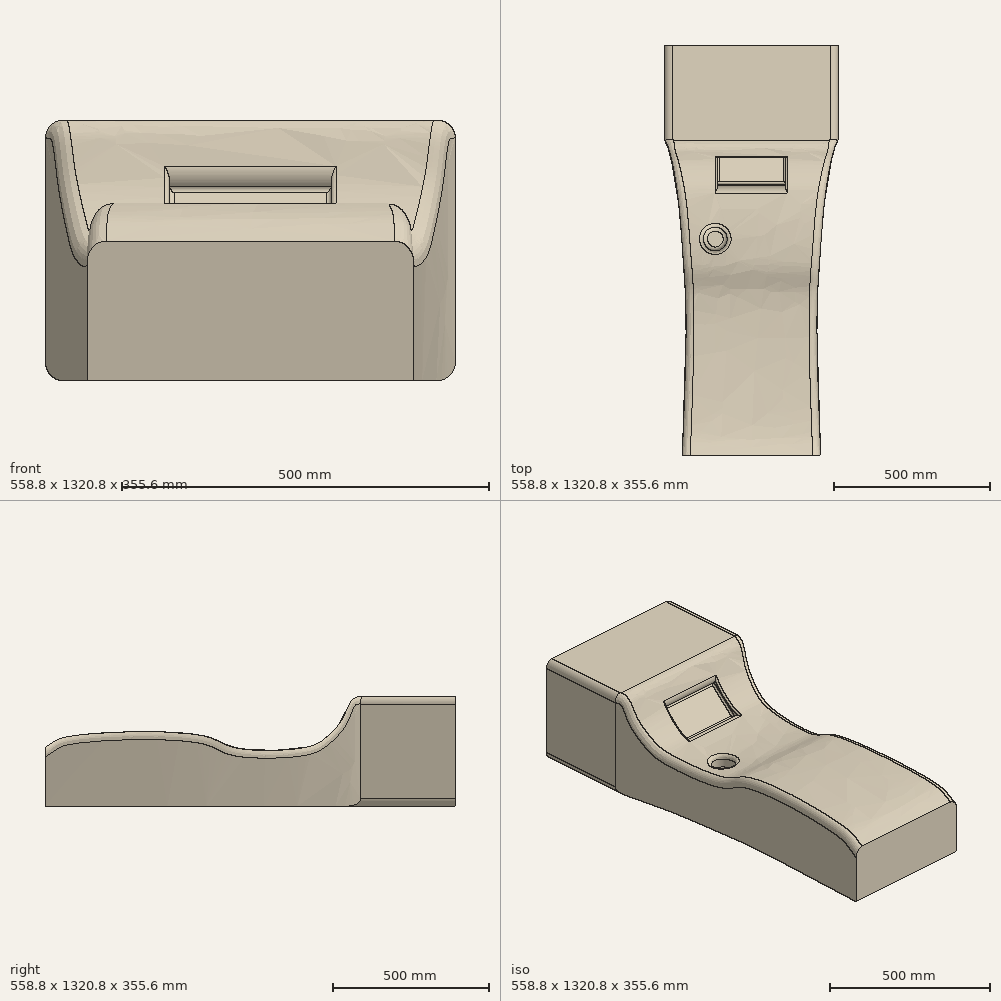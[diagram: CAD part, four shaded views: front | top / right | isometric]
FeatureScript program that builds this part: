
annotation { "Feature Type Name" : "Feature", "Feature Type Description" : "" }
export const myFeature = defineFeature(function(context is Context, id is Id, definition is map)
    precondition{}
    {
        {
            var Q0;
            Q0=qCreatedBy(makeId("Front.planeOp"),FACE);
            cPlane(context, id + "F0", {"entities" : qUnion([Q0]), "cplaneType" : CPlaneType.OFFSET, "offset" : 1016 * mm, "oppositeDirection" : true, "width" : 152.4 * mm, "height" : 152.4 * mm});
        }
        {
            var Q0;
            Q0=qCreatedBy(id+"F0.planeOp",FACE);
            var sketch = newSketch(context, id + "F1", { "sketchPlane" : qUnion([Q0])});
            skPoint(sketch, "E0.0", {"position": v(0, 165.1) * mm});
            skLineSegment(sketch, "E1", {"start": v(0, 165.1) * mm, "end": v(279.4, 165.1) * mm});
            skLineSegment(sketch, "E2", {"start": v(279.4, 165.1) * mm, "end": v(279.4, -190.5) * mm});
            skLineSegment(sketch, "E3", {"start": v(279.4, -190.5) * mm, "end": v(0, -190.5) * mm});
            skLineSegment(sketch, "E4", {"start": v(0, 165.1) * mm, "end": v(-279.4, 165.1) * mm});
            skLineSegment(sketch, "E5", {"start": v(-279.4, 165.1) * mm, "end": v(-279.4, -190.5) * mm});
            skLineSegment(sketch, "E6", {"start": v(-279.4, -190.5) * mm, "end": v(0, -190.5) * mm});
            skSolve(sketch);
        }
        {
            var Q0;
            Q0=qCreatedBy(makeId("Right.planeOp"),FACE);
            var sketch = newSketch(context, id + "F2", { "sketchPlane" : qUnion([Q0])});
            skFitSpline(sketch, "E7", {"points": [v(0, 0) * mm, v(24.74, 16.6) * mm, v(49, 28.94) * mm, v(187.46, 47.43) * mm, v(521.37, 34.71) * mm, v(607.94, 0) * mm, v(838.07, 0) * mm, v(901.63, 29.24) * mm, v(960.8, 98.27) * mm, v(1016, 165.1) * mm], "startDerivative": vector(273.3, 180.11) * mm, "endDerivative": vector(1078.66, 86.3) * mm});
            skLineSegment(sketch, "E8", {"start": v(0, 0) * mm, "end": v(0, 310.78) * mm});
            skLineSegment(sketch, "E9", {"start": v(0, 310.78) * mm, "end": v(1016, 310.78) * mm});
            skLineSegment(sketch, "E10", {"start": v(1016, 310.78) * mm, "end": v(1016, 165.1) * mm});
            skSolve(sketch);
        }
        {
            var Q0;
            Q0 = qSketchRegion(id + "F1", true);
            extrude(context, id + "F3", {"entities" : qUnion([Q0]), "depth" : 1016 * mm, "offsetDistance" : 25.4 * mm});
        }
        {
            var Q0;
            Q0=makeQuery(id+"F2.imprint","IMPRINT",FACE,{"disambiguationData":[TD([[makeQuery(id+"F2.imprint","IMPRINT",EDGE,{"derivedFrom":sQuery(id+"F2.wireOp",EDGE,"E7")}),1.0]])]});
            extrude(context, id + "F4", {"entities" : qUnion([Q0]), "operationType" : NewBodyOperationType.REMOVE, "endBound" : BoundingType.SYMMETRIC, "depth" : 1016 * mm, "offsetDistance" : 25.4 * mm});
        }
        {
            var Q0;
            Q0=qCreatedBy(makeId("Top.planeOp"),FACE);
            var sketch = newSketch(context, id + "F5", { "sketchPlane" : qUnion([Q0])});
            skLineSegment(sketch, "E11", {"start": v(279.4, 1016) * mm, "end": v(-279.4, 1016) * mm});
            skPoint(sketch, "E12.0", {"position": v(-222.79, 0) * mm});
            skLineSegment(sketch, "E13", {"start": v(0, 0) * mm, "end": v(-222.79, 0) * mm});
            skFitSpline(sketch, "E14", {"points": [v(-222.79, 0) * mm, v(-210.88, 448.78) * mm, v(-222.09, 661.6) * mm, v(-238.88, 845.63) * mm, v(-279.4, 1016) * mm], "startDerivative": vector(40.64, 1158.52) * mm, "endDerivative": vector(-221.68, 293.58) * mm});
            skLineSegment(sketch, "E15", {"start": v(-279.4, 1016) * mm, "end": v(-279.4, 0) * mm});
            skLineSegment(sketch, "E16", {"start": v(-222.79, 0) * mm, "end": v(-279.4, 0) * mm});
            skLineSegment(sketch, "E17.0", {"start": v(279.4, 0) * mm, "end": v(-279.4, 0) * mm});
            skFitSpline(sketch, "E18.0", {"points": [v(279.4, 1016) * mm, v(279.4, 979.93) * mm, v(279.4, 970.1) * mm, v(279.4, 900.22) * mm, v(279.4, 844.06) * mm, v(279.4, 591.76) * mm, v(279.4, 534.2) * mm, v(279.4, 191.24) * mm, v(279.4, 51.87) * mm, v(279.4, 26.72) * mm, v(279.4, 5.36) * mm, v(279.4, 0) * mm]});
            skFitSpline(sketch, "E19.MirrorCS", {"points": [v(222.79, 0) * mm, v(210.88, 448.78) * mm, v(222.09, 661.6) * mm, v(238.88, 845.63) * mm, v(279.4, 1016) * mm], "startDerivative": vector(-40.64, 1158.52) * mm, "endDerivative": vector(221.68, 293.58) * mm});
            skSolve(sketch);
        }
        {
            var Q0;
            {var subQ0=sQuery(id+"F5.wireOp",EDGE,"E14");Q0=makeQuery(id+"F5.imprint","IMPRINT",FACE,{"disambiguationData":[TD([[makeQuery(id+"F5.imprint","IMPRINT",EDGE,{"derivedFrom":subQ0}),1.0]])]});}
            var Q1;
            {var subQ0=sQuery(id+"F5.wireOp",EDGE,"E18.0");Q1=makeQuery(id+"F5.imprint","IMPRINT",FACE,{"disambiguationData":[TD([[makeQuery(id+"F5.imprint","IMPRINT",EDGE,{"derivedFrom":subQ0}),-1.0]])]});}
            extrude(context, id + "F6", {"entities" : qUnion([Q0, Q1]), "operationType" : NewBodyOperationType.REMOVE, "endBound" : BoundingType.SYMMETRIC, "oppositeDirection" : true, "depth" : 508 * mm, "offsetDistance" : 25.4 * mm});
        }
        {
            var Q0;
            Q0=makeQuery(id+"F1.imprint","IMPRINT",FACE,{"disambiguationData":[TD([[makeQuery(id+"F1.imprint","IMPRINT",EDGE,{"derivedFrom":sQuery(id+"F1.wireOp",EDGE,"E1")}),-1.0]])]});
            var sketch = newSketch(context, id + "F7", { "sketchPlane" : qUnion([Q0])});
            skLineSegment(sketch, "E20.0", {"start": v(0, 165.1) * mm, "end": v(279.4, 165.1) * mm});
            skLineSegment(sketch, "E21.0", {"start": v(0, 165.1) * mm, "end": v(-279.4, 165.1) * mm});
            skLineSegment(sketch, "E22.0", {"start": v(-279.4, 165.1) * mm, "end": v(-279.4, -190.5) * mm});
            skLineSegment(sketch, "E23.0", {"start": v(-279.4, -190.5) * mm, "end": v(0, -190.5) * mm});
            skLineSegment(sketch, "E24.0", {"start": v(279.4, -190.5) * mm, "end": v(0, -190.5) * mm});
            skLineSegment(sketch, "E25.0", {"start": v(279.4, 165.1) * mm, "end": v(279.4, -190.5) * mm});
            skLineSegment(sketch, "E26.bottom", {"start": v(279.4, 165.1) * mm, "end": v(-279.4, 165.1) * mm});
            skLineSegment(sketch, "E26.top", {"start": v(279.4, -190.5) * mm, "end": v(-279.4, -190.5) * mm});
            skSolve(sketch);
        }
        {
            var Q0;
            {var subQ3=sQuery(id+"F7.wireOp",EDGE,"E25.0");Q0=makeQuery(id+"F7.imprint","IMPRINT",FACE,{"disambiguationData":[TD([[makeQuery(id+"F7.imprint","IMPRINT",EDGE,{"derivedFrom":subQ3}),-1.0]])]});}
            extrude(context, id + "F8", {"entities" : qUnion([Q0]), "operationType" : NewBodyOperationType.ADD, "oppositeDirection" : true, "depth" : 304.8 * mm, "offsetDistance" : 25.4 * mm});
        }
        {
            var Q0;
            Q0=makeQuery(id+"F8.opExtrude","SWEPT_EDGE",EDGE,{"disambiguationData":[OSD([sQuery(id+"F7.wireOp",EDGE,"E26.bottom"),sQuery(id+"F7.wireOp",EDGE,"E22.0")])]});
            var Q1;
            Q1=makeQuery(id+"F6.boolean.opBoolean","INTERSECT",EDGE,{"derivedFrom":[makeQuery(id+"F4.boolean.opBoolean","COPY",FACE,{"derivedFrom":makeQuery(id+"F4.opExtrude","SWEPT_FACE",FACE,{"disambiguationData":[OSD([sQuery(id+"F2.wireOp",EDGE,"E7")])]})}),makeQuery(id+"F6.opExtrude","SWEPT_FACE",FACE,{"disambiguationData":[OSD([sQuery(id+"F5.wireOp",EDGE,"E14")])]})]});
            var Q2;
            Q2=makeQuery(id+"F8.opExtrude","SWEPT_EDGE",EDGE,{"disambiguationData":[OSD([sQuery(id+"F7.wireOp",EDGE,"E26.bottom"),sQuery(id+"F7.wireOp",EDGE,"E25.0")])]});
            var Q3;
            Q3=makeQuery(id+"F6.boolean.opBoolean","INTERSECT",EDGE,{"derivedFrom":[makeQuery(id+"F4.boolean.opBoolean","COPY",FACE,{"derivedFrom":makeQuery(id+"F4.opExtrude","SWEPT_FACE",FACE,{"disambiguationData":[OSD([sQuery(id+"F2.wireOp",EDGE,"E7")])]})}),makeQuery(id+"F6.opExtrude","SWEPT_FACE",FACE,{"disambiguationData":[OSD([sQuery(id+"F5.wireOp",EDGE,"E19.MirrorCS")])]})]});
            var Q4;
            Q4=makeQuery(id+"F4.boolean.opBoolean","COPY",EDGE,{"derivedFrom":makeQuery(id+"F4.opExtrude","SWEPT_EDGE",EDGE,{"disambiguationData":[OSD([sQuery(id+"F2.wireOp",EDGE,"E7"),sQuery(id+"F2.wireOp",EDGE,"E8")])]})});
            var Q5;
            Q5=makeQuery(id+"F6.boolean.opBoolean","COPY",EDGE,{"derivedFrom":makeQuery(id+"F6.opExtrude","SWEPT_EDGE",EDGE,{"disambiguationData":[OSD([sQuery(id+"F5.wireOp",EDGE,"E17.0"),sQuery(id+"F5.wireOp",EDGE,"E19.MirrorCS")])]})});
            var Q6;
            Q6=makeQuery(id+"F6.boolean.opBoolean","COPY",EDGE,{"derivedFrom":makeQuery(id+"F6.opExtrude","SWEPT_EDGE",EDGE,{"disambiguationData":[OSD([sQuery(id+"F5.wireOp",EDGE,"E14"),sQuery(id+"F5.wireOp",EDGE,"E17.0")])]})});
            fillet(context, id + "F9", {"entities" : qUnion([Q0, Q1, Q2, Q3, Q4, Q5, Q6]), "radius" : 25.4 * mm, "tangentPropagation" : true, "allowEdgeOverflow" : false});
        }
        {
            var Q0;
            Q0=qCreatedBy(makeId("Top.planeOp"),FACE);
            var sketch = newSketch(context, id + "F10", { "sketchPlane" : qUnion([Q0])});
            skLineSegment(sketch, "E27", {"start": v(-218, 696.98) * mm, "end": v(214.2, 696.98) * mm, "construction": true});
            skCircle(sketch, "E28", {"center": v(-116.4, 696.98) * mm, "radius": 38.1 * mm});
            skLineSegment(sketch, "E29.0", {"start": v(-196.46, 11.18) * mm, "end": v(196.46, 11.18) * mm});
            skSolve(sketch);
        }
        {
            var Q0;
            Q0 = qSketchRegion(id + "F10", true);
            extrude(context, id + "F11", {"entities" : qUnion([Q0]), "operationType" : NewBodyOperationType.REMOVE, "oppositeDirection" : true, "depth" : 63.5 * mm, "offsetDistance" : 25.4 * mm});
        }
        {
            var Q0;
            Q0=makeQuery(id+"F11.boolean.opBoolean","INTERSECT",EDGE,{"derivedFrom":[makeQuery(id+"F4.boolean.opBoolean","COPY",FACE,{"derivedFrom":makeQuery(id+"F4.opExtrude","SWEPT_FACE",FACE,{"disambiguationData":[OSD([sQuery(id+"F2.wireOp",EDGE,"E7")])]})}),makeQuery(id+"F11.opExtrude","SWEPT_FACE",FACE,{"disambiguationData":[OSD([sQuery(id+"F10.wireOp",EDGE,"E28")])]})]});
            var Q1;
            Q1=makeQuery(id+"F11.boolean.opBoolean","COPY",EDGE,{"derivedFrom":makeQuery(id+"F11.opExtrude","CAP_EDGE",EDGE,{"disambiguationData":[OSD([sQuery(id+"F10.wireOp",EDGE,"E28")])],"isStart":false})});
            var Q2;
            Q2=makeQuery(id+"FA7N4mf670c91CE_1.1.F11.boolean.opBoolean","INTERSECT",EDGE,{"derivedFrom":[makeQuery(id+"F4.boolean.opBoolean","COPY",FACE,{"derivedFrom":makeQuery(id+"F4.opExtrude","SWEPT_FACE",FACE,{"disambiguationData":[OSD([sQuery(id+"F2.wireOp",EDGE,"E7")])]})}),makeQuery(id+"FA7N4mf670c91CE_1.1.F11.opExtrude","SWEPT_FACE",FACE,{"disambiguationData":[OSD([sQuery(id+"F10.wireOp",EDGE,"E28")])]})]});
            var Q3;
            Q3=makeQuery(id+"FA7N4mf670c91CE_1.1.F11.boolean.opBoolean","COPY",EDGE,{"derivedFrom":makeQuery(id+"FA7N4mf670c91CE_1.1.F11.opExtrude","CAP_EDGE",EDGE,{"disambiguationData":[OSD([sQuery(id+"F10.wireOp",EDGE,"E28")])],"isStart":false})});
            fillet(context, id + "F12", {"entities" : qUnion([Q0, Q1, Q2, Q3]), "radius" : 12.7 * mm, "tangentPropagation" : true, "allowEdgeOverflow" : false});
        }
        {
            var Q0;
            Q0=sQuery(id+"F1.wireOp",EDGE,"E1");
            cPoint(context, id + "F13", {"entities" : qUnion([Q0]), "parameter" : 0.5});
        }
        {
            var Q0;
            Q0=sQuery(id+"F1.wireOp",EDGE,"E4");
            cPoint(context, id + "F14", {"entities" : qUnion([Q0]), "parameter" : 0.5});
        }
        {
            var Q0;
            Q0 = qCreatedBy(id + "F13" ,VERTEX);
            var Q1;
            Q1 = qCreatedBy(id + "F14" ,VERTEX);
            var Q2;
            Q2=sQuery(id+"F2.wireOp",VERTEX,"E7.6.internal");
            cPlane(context, id + "F15", {"entities" : qUnion([Q0, Q1, Q2]), "cplaneType" : CPlaneType.THREE_POINT, "offset" : 25.4 * mm, "width" : 152.4 * mm, "height" : 152.4 * mm});
        }
        {
            var Q0;
            Q0=qCreatedBy(id+"F15.planeOp",FACE);
            var sketch = newSketch(context, id + "F16", { "sketchPlane" : qUnion([Q0])});
            skLineSegment(sketch, "E30.bottom", {"start": v(-110.5, -758.55) * mm, "end": v(110.5, -758.55) * mm});
            skLineSegment(sketch, "E30.top", {"start": v(-110.5, -633.32) * mm, "end": v(110.5, -633.32) * mm});
            skLineSegment(sketch, "E30.left", {"start": v(-110.49, -758.55) * mm, "end": v(-110.5, -633.32) * mm});
            skLineSegment(sketch, "E30.right", {"start": v(110.5, -758.55) * mm, "end": v(110.5, -633.32) * mm});
            skSolve(sketch);
        }
        {
            var Q0;
            Q0 = qSketchRegion(id + "F16", true);
            extrude(context, id + "F17", {"entities" : qUnion([Q0]), "operationType" : NewBodyOperationType.REMOVE, "depth" : 38.1 * mm, "offsetDistance" : 25.4 * mm});
        }
        {
            var Q0;
            Q0=makeQuery(id+"F17.boolean.opBoolean","INTERSECT",EDGE,{"derivedFrom":[makeQuery(id+"F4.boolean.opBoolean","COPY",FACE,{"derivedFrom":makeQuery(id+"F4.opExtrude","SWEPT_FACE",FACE,{"disambiguationData":[OSD([sQuery(id+"F2.wireOp",EDGE,"E7")])]})}),makeQuery(id+"F17.opExtrude","SWEPT_FACE",FACE,{"disambiguationData":[OSD([sQuery(id+"F16.wireOp",EDGE,"E30.right")])]})]});
            var Q1;
            Q1=makeQuery(id+"F17.boolean.opBoolean","INTERSECT",EDGE,{"derivedFrom":[makeQuery(id+"F4.boolean.opBoolean","COPY",FACE,{"derivedFrom":makeQuery(id+"F4.opExtrude","SWEPT_FACE",FACE,{"disambiguationData":[OSD([sQuery(id+"F2.wireOp",EDGE,"E7")])]})}),makeQuery(id+"F17.opExtrude","SWEPT_FACE",FACE,{"disambiguationData":[OSD([sQuery(id+"F16.wireOp",EDGE,"E30.left")])]})]});
            var Q2;
            Q2=makeQuery(id+"F17.boolean.opBoolean","COPY",EDGE,{"derivedFrom":makeQuery(id+"F17.opExtrude","CAP_EDGE",EDGE,{"disambiguationData":[OSD([sQuery(id+"F16.wireOp",EDGE,"E30.right")])],"isStart":false})});
            var Q3;
            Q3=makeQuery(id+"F17.boolean.opBoolean","COPY",EDGE,{"derivedFrom":makeQuery(id+"F17.opExtrude","CAP_EDGE",EDGE,{"disambiguationData":[OSD([sQuery(id+"F16.wireOp",EDGE,"E30.top")])],"isStart":false})});
            var Q4;
            Q4=makeQuery(id+"F17.boolean.opBoolean","COPY",EDGE,{"derivedFrom":makeQuery(id+"F17.opExtrude","CAP_EDGE",EDGE,{"disambiguationData":[OSD([sQuery(id+"F16.wireOp",EDGE,"E30.left")])],"isStart":false})});
            var Q5;
            Q5=makeQuery(id+"F17.boolean.opBoolean","COPY",EDGE,{"derivedFrom":makeQuery(id+"F17.opExtrude","CAP_EDGE",EDGE,{"disambiguationData":[OSD([sQuery(id+"F16.wireOp",EDGE,"E30.bottom")])],"isStart":false})});
            fillet(context, id + "F18", {"entities" : qUnion([Q0, Q1, Q2, Q3, Q4, Q5]), "radius" : 6.35 * mm, "allowEdgeOverflow" : false});
        }
        {
            var Q0;
            Q0=makeQuery(id+"F17.boolean.opBoolean","INTERSECT",EDGE,{"derivedFrom":[makeQuery(id+"F4.boolean.opBoolean","COPY",FACE,{"derivedFrom":makeQuery(id+"F4.opExtrude","SWEPT_FACE",FACE,{"disambiguationData":[OSD([sQuery(id+"F2.wireOp",EDGE,"E7")])]})}),makeQuery(id+"F17.opExtrude","SWEPT_FACE",FACE,{"disambiguationData":[OSD([sQuery(id+"F16.wireOp",EDGE,"E30.bottom")])]})]});
            var Q1;
            Q1=makeQuery(id+"F17.boolean.opBoolean","INTERSECT",EDGE,{"derivedFrom":[makeQuery(id+"F4.boolean.opBoolean","COPY",FACE,{"derivedFrom":makeQuery(id+"F4.opExtrude","SWEPT_FACE",FACE,{"disambiguationData":[OSD([sQuery(id+"F2.wireOp",EDGE,"E7")])]})}),makeQuery(id+"F17.opExtrude","SWEPT_FACE",FACE,{"disambiguationData":[OSD([sQuery(id+"F16.wireOp",EDGE,"E30.top")])]})]});
            fillet(context, id + "F19", {"entities" : qUnion([Q0, Q1]), "radius" : 25.4 * mm, "tangentPropagation" : true, "allowEdgeOverflow" : false});
        }
        {
            var Q0;
            Q0=makeQuery(id+"F8.boolean.opBoolean","MERGE",FACE,{"derivedFrom":[makeQuery(id+"F3.opExtrude","SWEPT_FACE",FACE,{"disambiguationData":[OSD([sQuery(id+"F1.wireOp",EDGE,"E3"),sQuery(id+"F1.wireOp",EDGE,"E6")])]}),makeQuery(id+"F8.opExtrude","SWEPT_FACE",FACE,{"disambiguationData":[OSD([sQuery(id+"F7.wireOp",EDGE,"E26.top")])]})]});
            shell(context, id + "F20", {"entities" : qUnion([Q0]), "thickness" : 12.7 * mm});
        }
    });
